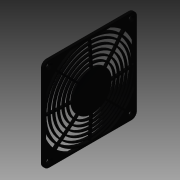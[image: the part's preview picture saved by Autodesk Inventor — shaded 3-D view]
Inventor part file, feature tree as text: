
AUTODESK INVENTOR PART (.ipt)
format: ipt  version: 2016 SP1 (Build 200210100, 210)  size: 891,392 bytes
history: native  units: mm
features: sketch x5, extrude x4, other x4, projected_geometry x3, plane x2, revolve x2, pattern_circular x2, fillet x2, hole x1
ambient origin geometry x8: Origin, YZ Plane, XZ Plane, XY Plane, X Axis, Y Axis, Z Axis, Center Point
bodies: Solid1 (feature_tree)
feature tree (25):
  extrude  "Extrusion1"  Depth=119.0mm
  sketch  "Sketch2"  dims[d2=3.8mm d3=0.0mm d4=105.0mm]
  plane  "Work Plane2"
  sketch  "Sketch3"  dims[d5=52.5mm d6=105.0mm]
  revolve  "Revolution2"  [1 undecoded]
  revolve  "Revolution3"  [1 undecoded]
  hole  "Hole2"  [1 undecoded]
  plane  "Work Plane3"
  sketch  "Sketch6"  dims[d9=59.5mm d67=3.5mm d68=3.5mm d69=119.0mm d70=59.5mm d72=1.0mm d74=90.0deg d75=90.0deg d76=4.5mm d77=6.0mm d78=8.0mm d79=2.0mm d80=90.0deg d81=8.0mm d82=20.594885mm d139=50.0mm d140=4.0mm d141=1.5mm d142=4.0mm d143=1.5mm d144=4.0mm d145=1.5mm d146=4.0mm d147=1.5mm d148=4.0mm d149=1.5mm d155=2.0mm d156=1.0mm d157=3.8mm d158=0.0mm d160=4.0mm d173=40.0mm d175=360.0deg d180=56.5mm d181=40.0mm d183=360.0deg d190=10.0mm d191=0.0mm d192=40.0mm d193=360.0deg d196=7.0mm d198=2.0mm d199=1.0mm d211=10.0mm d212=0.0mm d213=80.0mm d214=360.0deg d216=0.5mm]
  extrude  "Extrusion3"  Depth=0.5mm
  extrude  "Extrusion4"  Depth=0.5mm
  other  "Work Axis1"
  pattern_circular  "Circular Pattern1"  [2 undecoded]
  fillet  "Fillet1"  Radius=59.5mm
  extrude  "Extrusion5"  Depth=0.5mm
  other  "Work Axis2"
  pattern_circular  "Circular Pattern2"  Angle=90.0deg  [1 undecoded]
  fillet  "Fillet2"  [1 undecoded]
  sketch  "Sketch1"  dims[d0=119.0mm d1=119.0mm]
  projected_geometry  "Projected Loop1"
  projected_geometry  "Projected Loop2"
  other  "Image1"
  sketch  "Sketch4"  dims[d7=52.5mm d8=119.0mm]
  other  "Image2"
  projected_geometry  "Projected Loop3"
note: 7 required parameter values undecoded (feature->parameter linkage not recoverable at this tier; creation-order binding heuristic only, values carry confidence <= 0.55)